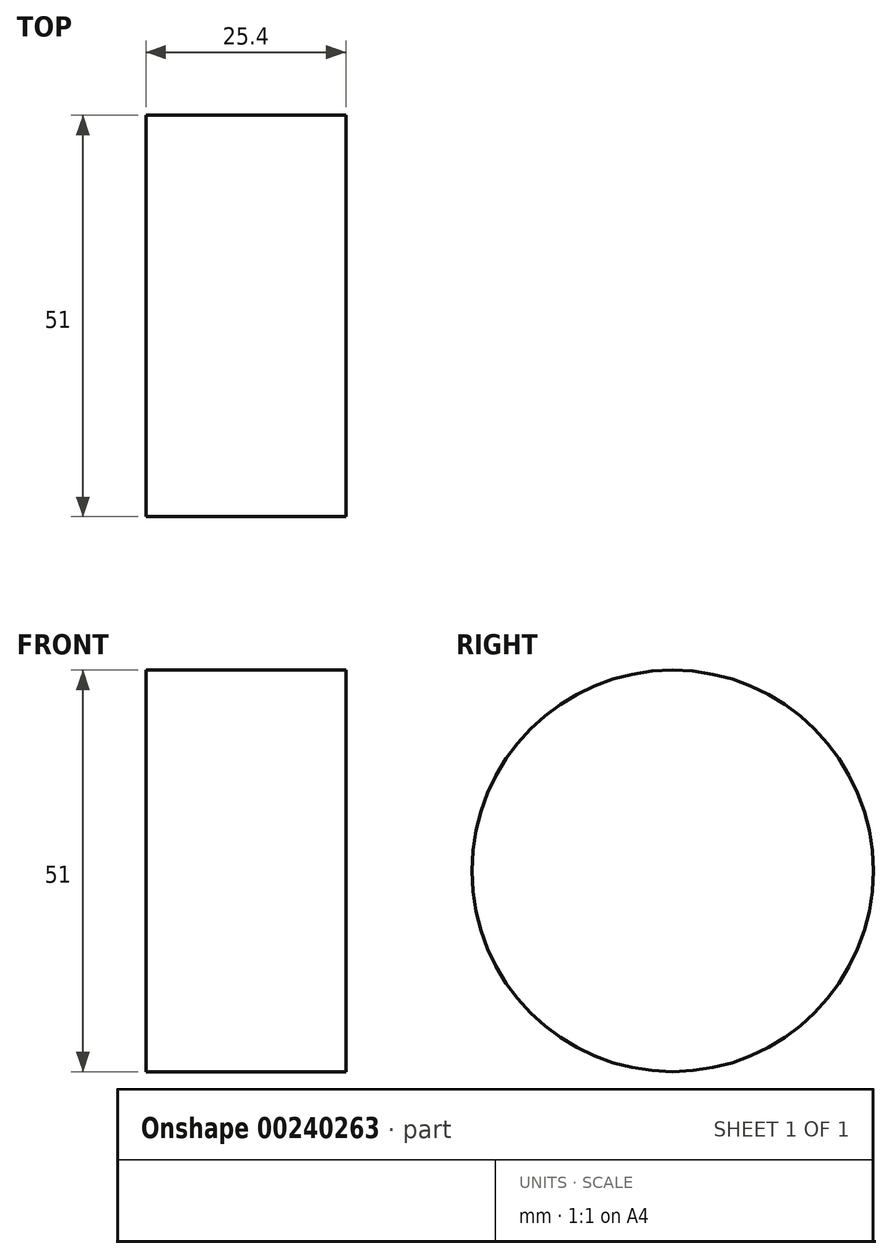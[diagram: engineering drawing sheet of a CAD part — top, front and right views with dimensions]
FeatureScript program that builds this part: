
annotation { "Feature Type Name" : "Feature", "Feature Type Description" : "" }
export const myFeature = defineFeature(function(context is Context, id is Id, definition is map)
    precondition{}
    {
        {
            var Q0;
            Q0=qCreatedBy(makeId("Right.planeOp"),FACE);
            var sketch = newSketch(context, id + "F0", { "sketchPlane" : qUnion([Q0])});
            skCircle(sketch, "E0", {"center": v(-33.16, 23.86) * mm, "radius": 25.5 * mm});
            skSolve(sketch);
        }
        {
            var Q0;
            Q0=makeQuery(id+"F0.imprint","IMPRINT",FACE,{"disambiguationData":[TD([[makeQuery(id+"F0.imprint","IMPRINT",EDGE,{"derivedFrom":sQuery(id+"F0.wireOp",EDGE,"E0")}),1.0]])]});
            extrude(context, id + "F1", {"entities" : qUnion([Q0]), "depth" : 25.4 * mm});
        }
    });
